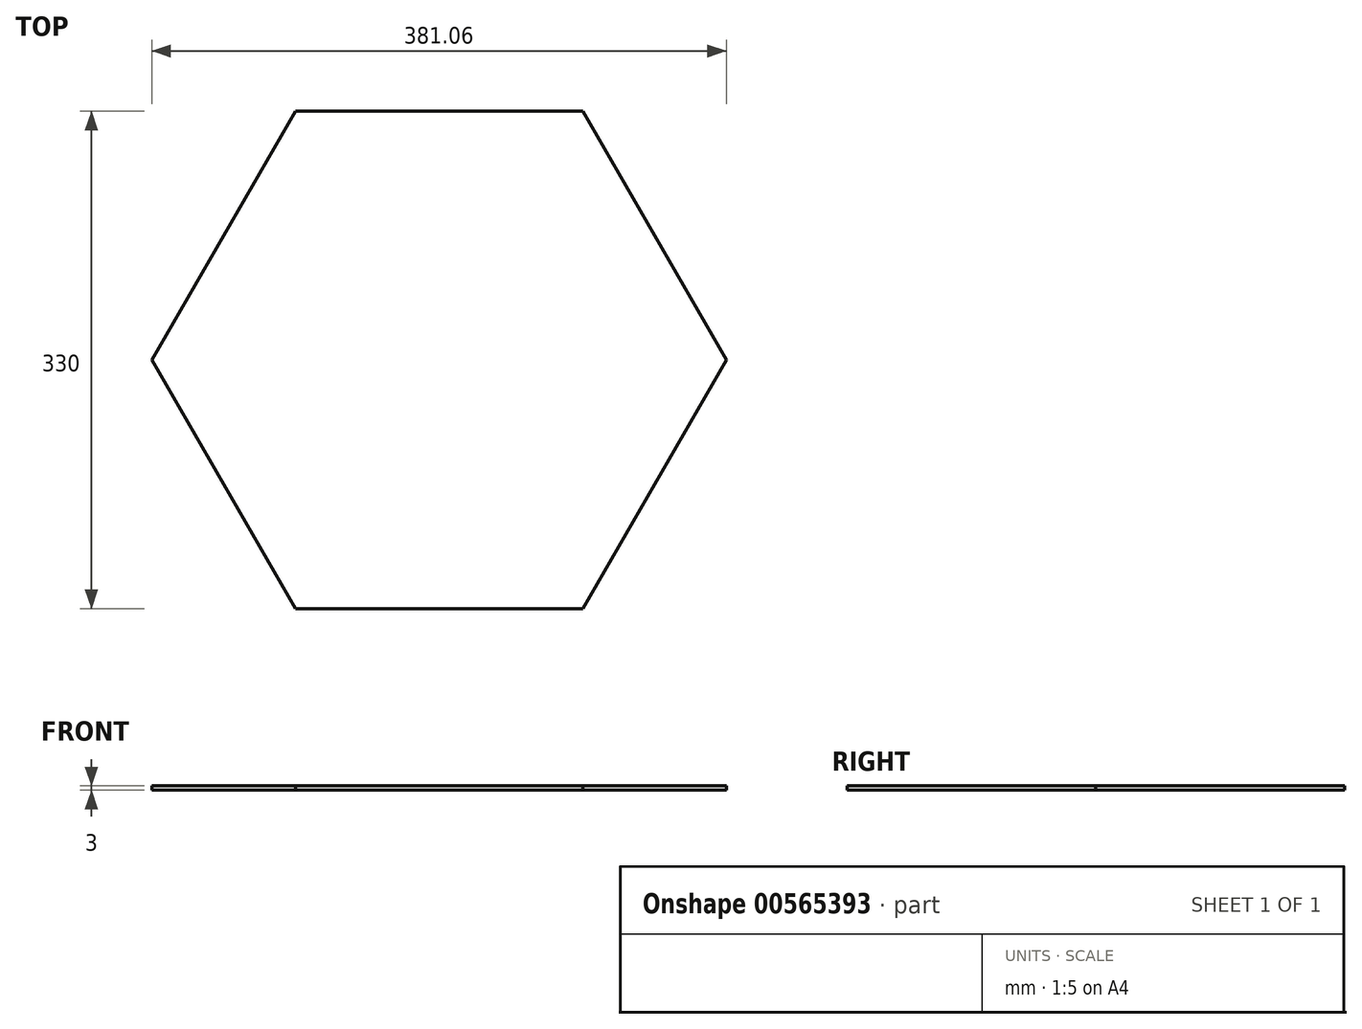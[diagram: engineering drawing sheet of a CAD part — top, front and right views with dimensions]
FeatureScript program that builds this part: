
annotation { "Feature Type Name" : "Feature", "Feature Type Description" : "" }
export const myFeature = defineFeature(function(context is Context, id is Id, definition is map)
    precondition{}
    {
        {
            var Q0;
            Q0=qCreatedBy(makeId("Top.planeOp"),FACE);
            var sketch = newSketch(context, id + "F0", { "sketchPlane" : qUnion([Q0])});
            skCircle(sketch, "E0.cCircle", {"center": v(0, 0) * mm, "radius": 165 * mm, "construction": true});
            skLineSegment(sketch, "E0.0", {"start": v(95.26, -165) * mm, "end": v(-95.26, -165) * mm});
            skLineSegment(sketch, "E0.1", {"start": v(-95.26, -165) * mm, "end": v(-190.53, 0) * mm});
            skLineSegment(sketch, "E0.2", {"start": v(-190.53, 0) * mm, "end": v(-95.26, 165) * mm});
            skLineSegment(sketch, "E0.3", {"start": v(-95.26, 165) * mm, "end": v(95.26, 165) * mm});
            skLineSegment(sketch, "E0.4", {"start": v(95.26, 165) * mm, "end": v(190.53, 0) * mm});
            skLineSegment(sketch, "E0.5", {"start": v(190.53, 0) * mm, "end": v(95.26, -165) * mm});
            skPoint(sketch, "E0.0.midPoint", {"position": v(0, -165) * mm});
            skSolve(sketch);
        }
        {
            var Q0;
            Q0=makeQuery(id+"F0.imprint","IMPRINT",FACE,{"disambiguationData":[TD([[makeQuery(id+"F0.imprint","IMPRINT",EDGE,{"derivedFrom":sQuery(id+"F0.wireOp",EDGE,"E0.0")}),-1.0]])]});
            extrude(context, id + "F1", {"entities" : qUnion([Q0]), "depth" : 3 * mm, "offsetDistance" : 25 * mm});
        }
    });
